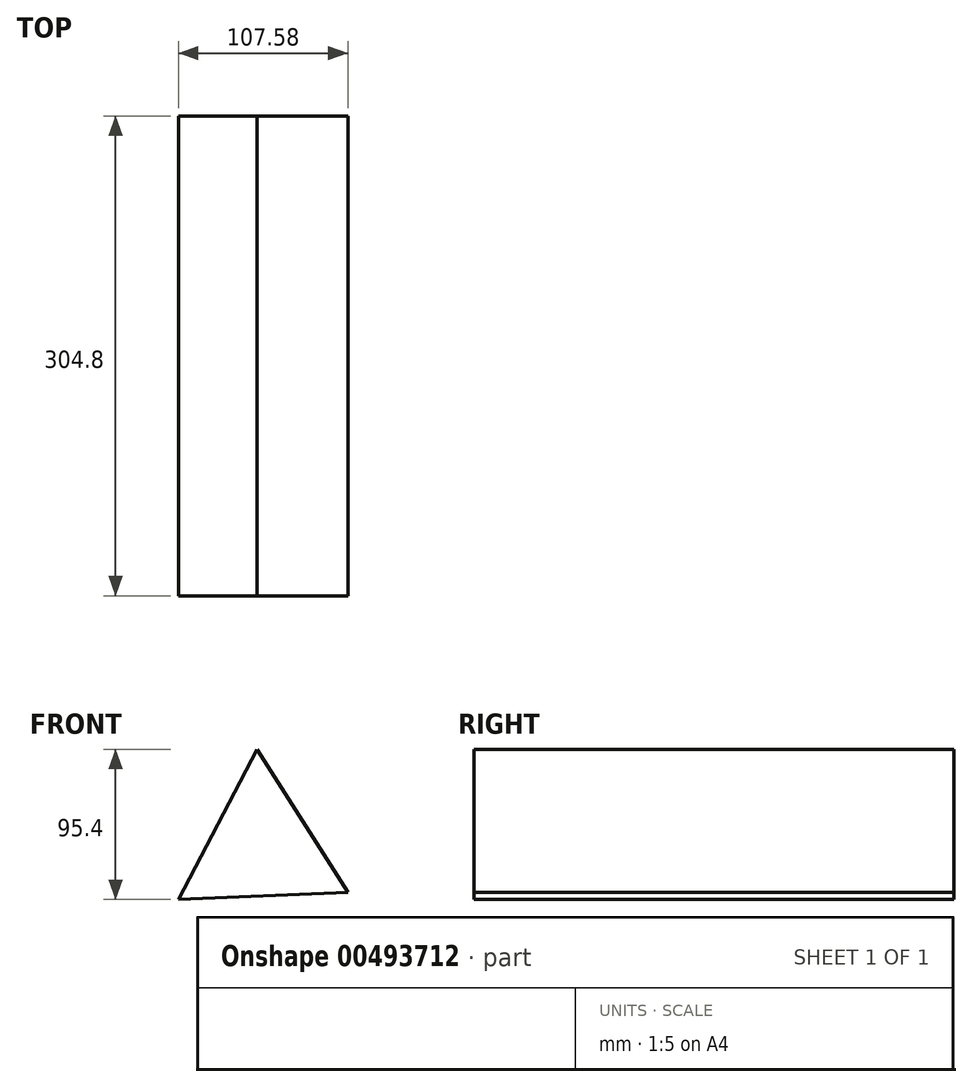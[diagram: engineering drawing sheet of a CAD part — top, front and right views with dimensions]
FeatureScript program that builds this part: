
annotation { "Feature Type Name" : "Feature", "Feature Type Description" : "" }
export const myFeature = defineFeature(function(context is Context, id is Id, definition is map)
    precondition{}
    {
        {
            var Q0;
            Q0=qCreatedBy(makeId("Front.planeOp"),FACE);
            var sketch = newSketch(context, id + "F0", { "sketchPlane" : qUnion([Q0])});
            skCircle(sketch, "E0.cCircle", {"center": v(0, 0) * mm, "radius": 62.16 * mm, "construction": true});
            skLineSegment(sketch, "E0.0", {"start": v(-2.58, 62.11) * mm, "end": v(55.08, -28.82) * mm});
            skLineSegment(sketch, "E0.1", {"start": v(55.08, -28.82) * mm, "end": v(-52.5, -33.3) * mm});
            skLineSegment(sketch, "E0.2", {"start": v(-52.5, -33.3) * mm, "end": v(-2.58, 62.11) * mm});
            skSolve(sketch);
        }
        {
            var Q0;
            Q0=makeQuery(id+"F0.imprint","IMPRINT",FACE,{"disambiguationData":[TD([[makeQuery(id+"F0.imprint","IMPRINT",EDGE,{"derivedFrom":sQuery(id+"F0.wireOp",EDGE,"E0.0")}),-1.0]])]});
            extrude(context, id + "F1", {"entities" : qUnion([Q0]), "depth" : 304.8 * mm});
        }
    });
